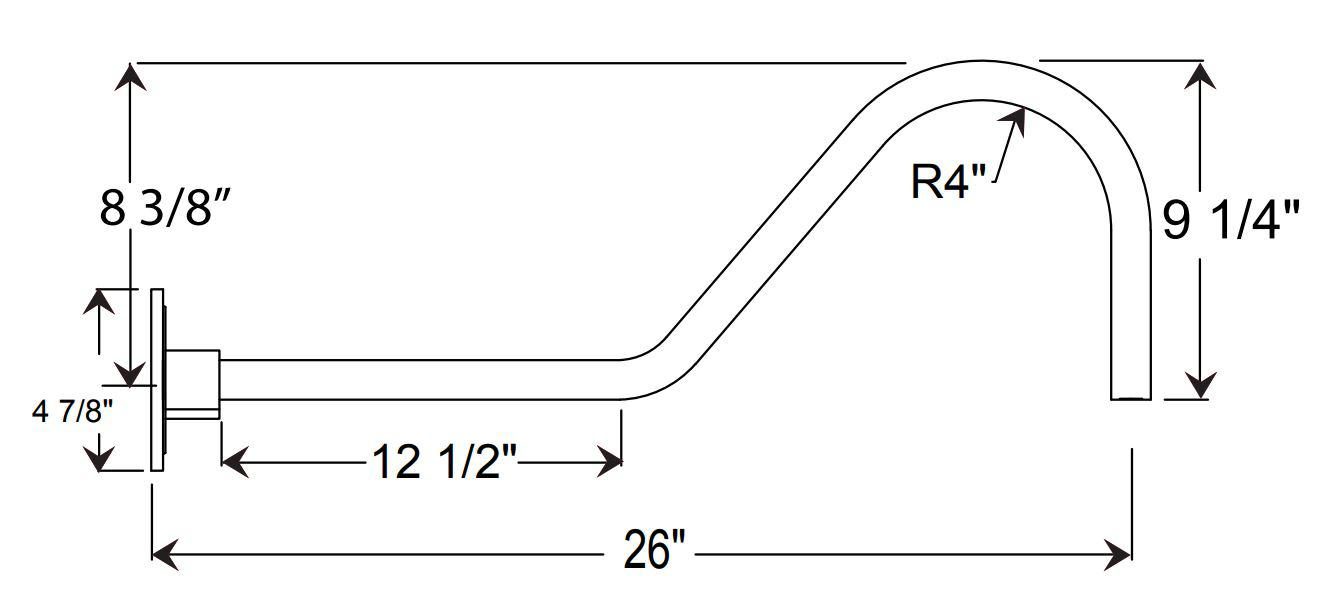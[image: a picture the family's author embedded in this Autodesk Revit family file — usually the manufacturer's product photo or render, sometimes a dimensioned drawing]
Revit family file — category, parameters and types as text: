
# Revit family: Orbitor T 200w -218,220 LED
name_source: partatom
category: Lighting Fixtures
units: mm (PartAtom-declared; Revit-internal decimal feet)

## family parameters
Always vertical = Yes
Cut with Voids When Loaded = No
Light Source = Yes
OmniClass Number = 23.80.70.00
OmniClass Title = Lighting
Part Type = Normal
Room Calculation Point = No
Round Connector Dimension = Use Diameter
Shared = No
Work Plane-Based = No

## types (2) — shared parameters
Apparent Load = 24 VA
Body Colour = Spun aluminium
Body Material = body
Bulb = Bulb
CRI = >90
Color Filter = 16777215
Construction Material = Heavy Duty spun aluminum.
Default Elevation = 0' - 0"
Description = 120-277 Voltage
Dimming = 1%
Dimming Lamp Color Temperature Shift = <None>
Efficiency = 65-125 lumens per watt
Fixture Height = 1' - 2"
INSIDE BODY = INSIDE BODY
Lamp = LED
Life = L70 50,000 hours
Load Classification = Lighting
Manufacturer = ANP Lighting
Photometric Web File = generic.ies
Power Factor = 1
Tilt Angle = 90.00°
URL = https://www.anplighting.com
Voltage = 277 V
Warranty = 5 year limited warranty
Wattage Comments = 24W

## per-type parameters (varying)
| type | Fixture Diameter | Model | ORBITOR18 | ORBITOR20 | Weight |
| ORB218 | 1' - 6" | ORBT218 | Yes | No | 3.0 lbs |
| ORB220 | 1' - 8" | ORBT220 | No | Yes | 3.5 lbs |

## geometry (parser evidence)
native form markers: Sweep x22
no freeform markers — native parametric forms only
